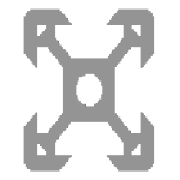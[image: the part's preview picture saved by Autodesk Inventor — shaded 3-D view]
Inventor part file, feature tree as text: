
AUTODESK INVENTOR PART (.ipt)
format: ipt  version: 2019 (Build 230136000, 136)  size: 200,192 bytes
history: native  units: mm
features: other x3, sketch x3, plane x1
ambient origin geometry x8: Origin, YZ Plane, XZ Plane, XY Plane, X Axis, Y Axis, Z Axis, Center Point
bodies: Solid1 (feature_tree), Body (feature_tree)
feature tree (7):
  other  "Driven Length"
  other  "Start Plane"
  other  "End Plane"
  sketch  "Sketch1"  dims[d2=4.2mm]
  sketch  "Sketch4"  dims[d3=1.5mm]
  plane  "Work Plane4"
  sketch  "Sketch5"  dims[d4=1.64mm d5=1.8mm d6=5.68mm d7=1.8mm d9=1.5mm d12=-0.0mm d13=400.0mm d14=0.13mm d15=0.0mm d18=90.0deg d17=400.0mm]
